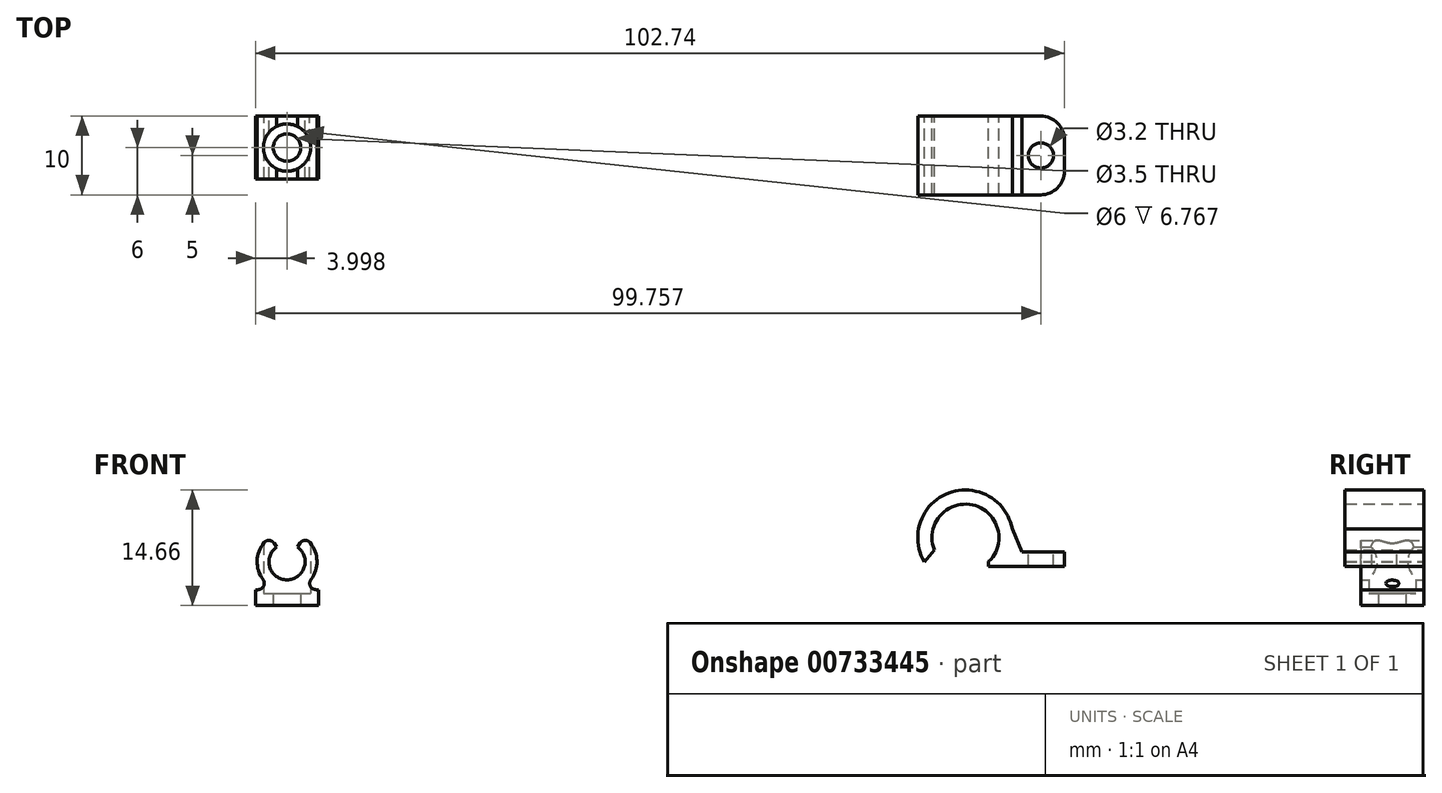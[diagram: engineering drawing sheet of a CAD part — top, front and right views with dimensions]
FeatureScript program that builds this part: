
annotation { "Feature Type Name" : "Feature", "Feature Type Description" : "" }
export const myFeature = defineFeature(function(context is Context, id is Id, definition is map)
    precondition{}
    {
        {
            var Q0;
            Q0=qCreatedBy(makeId("Front.planeOp"),FACE);
            var sketch = newSketch(context, id + "F0", { "sketchPlane" : qUnion([Q0])});
            skCircle(sketch, "E0", {"center": v(-55.02, 47.24) * mm, "radius": 2.3 * mm});
            skCircle(sketch, "E1", {"center": v(-55.02, 47.24) * mm, "radius": 3.8 * mm});
            skLineSegment(sketch, "E2", {"start": v(-55.02, 53.98) * mm, "end": v(-55.02, 29.88) * mm, "construction": true});
            skLineSegment(sketch, "E3", {"start": v(-55.02, 47.24) * mm, "end": v(-57.2, 50.35) * mm});
            skLineSegment(sketch, "E4", {"start": v(-55.02, 47.24) * mm, "end": v(-52.84, 50.35) * mm});
            skLineSegment(sketch, "E5.bottom", {"start": v(-59.02, 43.69) * mm, "end": v(-51.02, 43.69) * mm});
            skLineSegment(sketch, "E5.top", {"start": v(-59.02, 41.69) * mm, "end": v(-51.02, 41.69) * mm});
            skLineSegment(sketch, "E5.left", {"start": v(-59.02, 43.69) * mm, "end": v(-59.02, 41.69) * mm});
            skLineSegment(sketch, "E5.right", {"start": v(-51.02, 43.69) * mm, "end": v(-51.02, 41.69) * mm});
            skSolve(sketch);
        }
        {
            var Q0;
            {var subQ0=sQuery(id+"F0.wireOp",EDGE,"E3");var subQ1=sQuery(id+"F0.wireOp",EDGE,"E0");var subQ2=makeQuery(id+"F0.imprint","INTERSECT",VERTEX,{"derivedFrom":[subQ1,subQ0]});Q0=makeQuery(id+"F0.imprint","IMPRINT",FACE,{"disambiguationData":[TD([[makeQuery(id+"F0.imprint","IMPRINT",EDGE,{"disambiguationData":[TD([[subQ2,-1.0]])],"derivedFrom":subQ1}),-1.0]])]});}
            var Q1;
            Q1=makeQuery(id+"F0.imprint","IMPRINT",FACE,{"disambiguationData":[TD([[makeQuery(id+"F0.imprint","IMPRINT",EDGE,{"derivedFrom":sQuery(id+"F0.wireOp",EDGE,"E5.top")}),1.0]])]});
            var Q2;
            {var subQ0=sQuery(id+"F0.wireOp",EDGE,"E5.bottom");var subQ1=sQuery(id+"F0.wireOp",EDGE,"E1");var subQ2=makeQuery(id+"F0.imprint","INTERSECT",VERTEX,{"disambiguationData":[OD(0.0)],"derivedFrom":[subQ1,subQ0]});Q2=makeQuery(id+"F0.imprint","IMPRINT",FACE,{"disambiguationData":[TD([[makeQuery(id+"F0.imprint","IMPRINT",EDGE,{"disambiguationData":[TD([[subQ2,-1.0]])],"derivedFrom":subQ1}),1.0]])]});}
            extrude(context, id + "F1", {"entities" : qUnion([Q0, Q1, Q2]), "depth" : 8 * mm, "offsetDistance" : 25 * mm});
        }
        {
            var Q0;
            {var subQ0=sQuery(id+"F0.wireOp",EDGE,"E5.bottom");var subQ1=sQuery(id+"F0.wireOp",EDGE,"E1");Q0=makeQuery(id+"F1.opExtrude","SWEPT_EDGE",EDGE,{"disambiguationData":[OSD([subQ1,subQ0]),TDD([makeQuery(id+"F0.imprint","INTERSECT",VERTEX,{"disambiguationData":[OD(0.0)],"derivedFrom":[subQ1,subQ0]})])]});}
            var Q1;
            {var subQ0=sQuery(id+"F0.wireOp",EDGE,"E5.bottom");var subQ1=sQuery(id+"F0.wireOp",EDGE,"E1");Q1=makeQuery(id+"F1.opExtrude","SWEPT_EDGE",EDGE,{"disambiguationData":[OSD([subQ1,subQ0]),TDD([makeQuery(id+"F0.imprint","INTERSECT",VERTEX,{"disambiguationData":[OD(1.0)],"derivedFrom":[subQ1,subQ0]})])]});}
            var Q2;
            Q2=makeQuery(id+"F1.opExtrude","SWEPT_EDGE",EDGE,{"disambiguationData":[OSD([sQuery(id+"F0.wireOp",EDGE,"E1"),sQuery(id+"F0.wireOp",EDGE,"E3")])]});
            var Q3;
            Q3=makeQuery(id+"F1.opExtrude","SWEPT_EDGE",EDGE,{"disambiguationData":[OSD([sQuery(id+"F0.wireOp",EDGE,"E1"),sQuery(id+"F0.wireOp",EDGE,"E4")])]});
            fillet(context, id + "F2", {"entities" : qUnion([Q0, Q1, Q2, Q3]), "radius" : 0.8 * mm, "tangentPropagation" : true, "allowEdgeOverflow" : false});
        }
        {
            var Q0;
            Q0=makeQuery(id+"F1.opExtrude","SWEPT_FACE",FACE,{"disambiguationData":[OSD([sQuery(id+"F0.wireOp",EDGE,"E5.top")])]});
            var sketch = newSketch(context, id + "F3", { "sketchPlane" : qUnion([Q0])});
            skCircle(sketch, "E6", {"center": v(-55.02, 4) * mm, "radius": 1.75 * mm});
            skPoint(sketch, "E6.centerSnap0", {"position": v(-59.02, 4) * mm});
            skPoint(sketch, "E6.centerSnap1", {"position": v(-55.02, 8) * mm});
            skCircle(sketch, "E7", {"center": v(-55.02, 4) * mm, "radius": 3 * mm});
            skSolve(sketch);
        }
        {
            var Q0;
            Q0=makeQuery(id+"F3.imprint","IMPRINT",FACE,{"disambiguationData":[TD([[makeQuery(id+"F3.imprint","IMPRINT",EDGE,{"derivedFrom":sQuery(id+"F3.wireOp",EDGE,"E6")}),1.0]])]});
            extrude(context, id + "F4", {"entities" : qUnion([Q0]), "operationType" : NewBodyOperationType.REMOVE, "endBound" : BoundingType.THROUGH_ALL, "oppositeDirection" : true, "depth" : 25 * mm, "offsetDistance" : 25 * mm});
        }
        {
            var Q0;
            Q0=makeQuery(id+"F3.imprint","IMPRINT",FACE,{"disambiguationData":[TD([[makeQuery(id+"F3.imprint","IMPRINT",EDGE,{"derivedFrom":sQuery(id+"F3.wireOp",EDGE,"E6")}),-1.0]])]});
            extrude(context, id + "F5", {"entities" : qUnion([Q0]), "operationType" : NewBodyOperationType.REMOVE, "oppositeDirection" : true, "depth" : 15 * mm, "offsetDistance" : 25 * mm, "hasSecondDirection" : true, "secondDirectionOppositeDirection" : true, "secondDirectionDepth" : 1.5 * mm});
        }
        {
            var Q0;
            Q0=qCreatedBy(makeId("Front.planeOp"),FACE);
            var sketch = newSketch(context, id + "F6", { "sketchPlane" : qUnion([Q0])});
            skArc(sketch, "E8", {"start": v(34.1, 47.25) * mm, "mid": v(32.05, 54.45) * mm, "end": v(27.2, 48.74) * mm});
            skArc(sketch, "E9", {"start": v(37.1, 51.4) * mm, "mid": v(29.04, 55.97) * mm, "end": v(25.93, 47.24) * mm});
            skLineSegment(sketch, "E10.top", {"start": v(37.98, 46.67) * mm, "end": v(43.72, 46.67) * mm});
            skLineSegment(sketch, "E11", {"start": v(34.1, 47.25) * mm, "end": v(34.1, 46.67) * mm});
            skPoint(sketch, "E12.orphan", {"position": v(31.15, 68.3) * mm});
            skLineSegment(sketch, "E13.bottom", {"start": v(43.72, 46.67) * mm, "end": v(35.67, 46.67) * mm});
            skLineSegment(sketch, "E13.top", {"start": v(43.72, 48.47) * mm, "end": v(38.31, 48.47) * mm});
            skLineSegment(sketch, "E13.left", {"start": v(43.72, 46.67) * mm, "end": v(43.72, 48.47) * mm});
            skLineSegment(sketch, "E14", {"start": v(35.67, 46.67) * mm, "end": v(34.1, 46.67) * mm});
            skLineSegment(sketch, "E15", {"start": v(27.2, 48.74) * mm, "end": v(25.93, 47.24) * mm});
            skLineSegment(sketch, "E16", {"start": v(37.1, 51.4) * mm, "end": v(38.31, 48.47) * mm});
            skSolve(sketch);
        }
        {
            var Q0;
            Q0=makeQuery(id+"F6.imprint","IMPRINT",FACE,{"disambiguationData":[TD([[makeQuery(id+"F6.imprint","IMPRINT",EDGE,{"derivedFrom":sQuery(id+"F6.wireOp",EDGE,"E8")}),-1.0]])]});
            extrude(context, id + "F7", {"entities" : qUnion([Q0]), "depth" : 10 * mm, "offsetDistance" : 25 * mm});
        }
        {
            var Q0;
            Q0=makeQuery(id+"F7.opExtrude","SWEPT_FACE",FACE,{"disambiguationData":[OSD([sQuery(id+"F6.wireOp",EDGE,"E13.top")])]});
            var sketch = newSketch(context, id + "F8", { "sketchPlane" : qUnion([Q0])});
            skCircle(sketch, "E17", {"center": v(40.74, -5) * mm, "radius": 1.6 * mm});
            skPoint(sketch, "E18.startSnap0", {"position": v(40.74, 0) * mm});
            skPoint(sketch, "E19.startSnap0", {"position": v(43.15, -5) * mm});
            skLineSegment(sketch, "E20", {"start": v(40.74, 0) * mm, "end": v(40.74, -11.32) * mm, "construction": true});
            skLineSegment(sketch, "E21", {"start": v(45.2, -5) * mm, "end": v(23.55, -5) * mm, "construction": true});
            skSolve(sketch);
        }
        {
            var Q0;
            Q0=makeQuery(id+"F8.imprint","IMPRINT",FACE,{"disambiguationData":[TD([[makeQuery(id+"F8.imprint","IMPRINT",EDGE,{"derivedFrom":sQuery(id+"F8.wireOp",EDGE,"E17")}),1.0]])]});
            extrude(context, id + "F9", {"entities" : qUnion([Q0]), "operationType" : NewBodyOperationType.REMOVE, "endBound" : BoundingType.THROUGH_ALL, "oppositeDirection" : true, "depth" : 25 * mm, "offsetDistance" : 25 * mm});
        }
        {
            var Q0;
            Q0=makeQuery(id+"F7.opExtrude","CAP_EDGE",EDGE,{"disambiguationData":[OSD([sQuery(id+"F6.wireOp",EDGE,"E13.left")])],"isStart":false});
            var Q1;
            Q1=makeQuery(id+"F7.opExtrude","CAP_EDGE",EDGE,{"disambiguationData":[OSD([sQuery(id+"F6.wireOp",EDGE,"E13.left")])],"isStart":true});
            fillet(context, id + "F10", {"entities" : qUnion([Q0, Q1]), "radius" : 3 * mm, "tangentPropagation" : true, "allowEdgeOverflow" : false});
        }
    });
